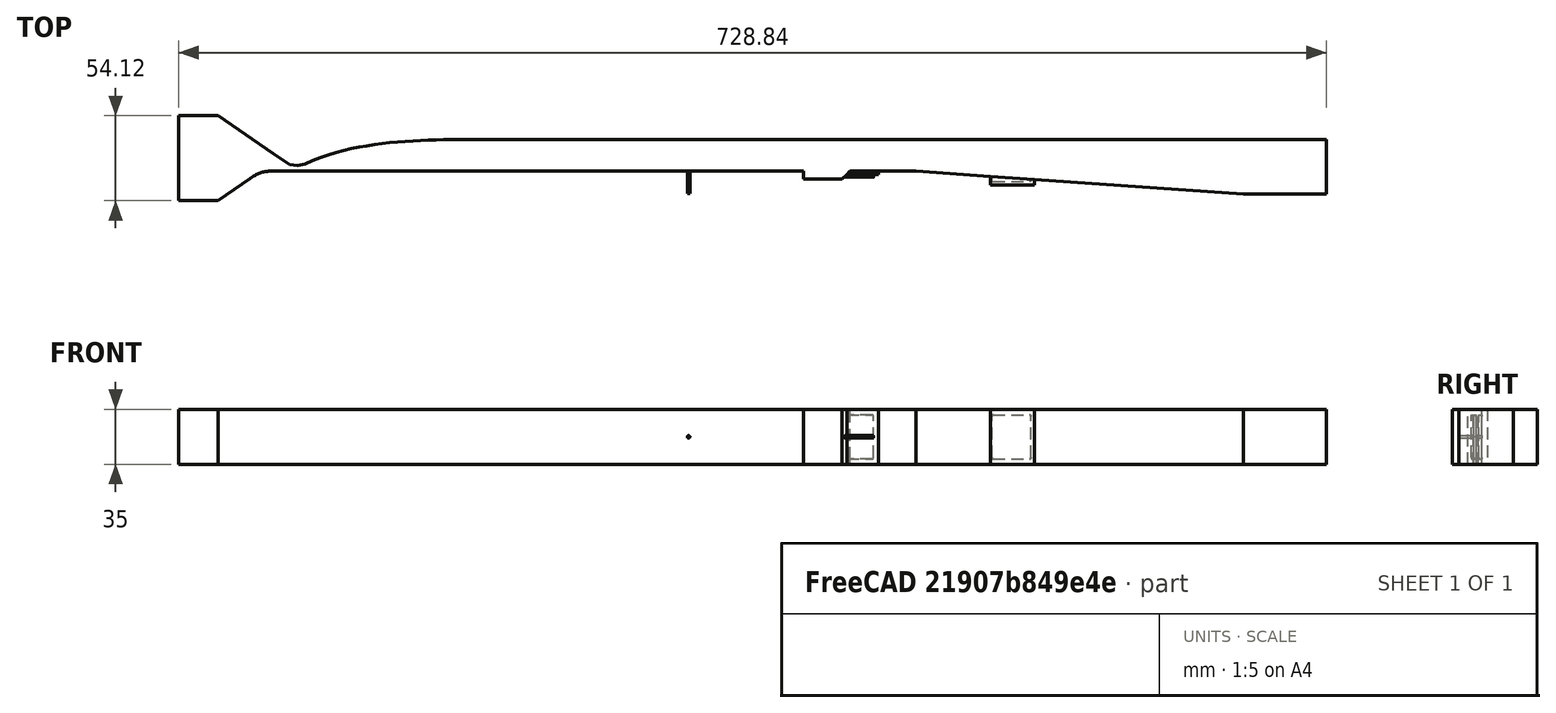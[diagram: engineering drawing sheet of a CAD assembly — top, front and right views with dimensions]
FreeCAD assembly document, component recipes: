
FREECAD ASSEMBLY — COMPONENT RECIPES ("actii")

This assembly document has 6 components, labeled P0..P5 below (a component is one placed body or linked part). 4 of them carry a construction recipe — the FreeCAD feature program that regenerates the part from scratch, quoted from this document or its linked companion documents; the rest are supplied as boundary geometry only. No exploded tour is included for this assembly.
COMPONENT P0 — recipe-attached ("Fluid001", modeled in this document).
Construction recipe (the document's own serialized feature program — sketch geometry with constraints, then the solid features built on it; lengths are millimeters unless a unit is written):

FEATURE [Sketcher::SketchObject] Sketch002  label="Fluid2DProfile001"
  FullyConstrained = true
  MapMode = 5
  Support = -> [XY_Plane001]
  sketch-geometry (16):
    g0: LineSegment StartX=209.437 StartY=27.0645 StartZ=0 EndX=234.437 EndY=27.0645 EndZ=0
    g1: BSplineCurve PolesCount=155 KnotsCount=153 Degree=3 IsPeriodic=0
    g2: LineSegment StartX=209.437 StartY=-27.0645 StartZ=0 EndX=234.437 EndY=-27.0645 EndZ=0
    g3: BSplineCurve PolesCount=28 KnotsCount=26 Degree=3 IsPeriodic=0
    g4: LineSegment StartX=383.28 StartY=11.6755 StartZ=0 EndX=938.28 EndY=11.6755 EndZ=0
    g5: LineSegment StartX=606.28 StartY=-8.32451 StartZ=0 EndX=606.28 EndY=-13.3245 EndZ=0
    g6: LineSegment StartX=606.28 StartY=-13.3245 StartZ=0 EndX=630.78 EndY=-13.3245 EndZ=0
    g7: LineSegment StartX=630.78 StartY=-13.3245 StartZ=0 EndX=635.78 EndY=-8.32451 EndZ=0
    g8: LineSegment StartX=635.78 StartY=-8.32451 StartZ=0 EndX=677.78 EndY=-8.32451 EndZ=0
    g9: LineSegment StartX=677.78 StartY=-8.32451 StartZ=0 EndX=885.78 EndY=-22.8693 EndZ=0
    g10: LineSegment StartX=938.28 StartY=11.6755 StartZ=0 EndX=938.28 EndY=-22.8693 EndZ=0
    g11: LineSegment StartX=885.78 StartY=-22.8693 StartZ=0 EndX=938.28 EndY=-22.8693 EndZ=0
    g12: LineSegment StartX=274.611 StartY=-8.32451 StartZ=0 EndX=606.28 EndY=-8.32451 EndZ=0
    g13: LineSegment StartX=269.437 StartY=2.95465 StartZ=0 EndX=234.437 EndY=27.0645 EndZ=0
    g14: LineSegment StartX=209.437 StartY=27.0645 StartZ=0 EndX=209.437 EndY=-27.0645 EndZ=0
    g15: LineSegment StartX=234.437 StartY=-27.0645 StartZ=0 EndX=254.652 EndY=-13.0512 EndZ=0
  constraints (44):
    c: Block(g1)
    c: Block(g3)
    c: DistanceX(g1,g4) = 555  'iso+cav+comb'
    c: Coincident(g4,g10)
    c: Vertical(g10)
    c: Coincident(g11,g10)
    c: Horizontal(g11)
    c: Coincident(g9,g8)
    c: Horizontal(g8)
    c: Horizontal(g6)
    c: Vertical(g5)
    c: Coincident(g11,g9)
    c: DistanceY(g5,g1) = 20
    c: Coincident(g8,g7)
    c: Horizontal(g4)
    c: DistanceX(g1,g5) = 223
    c: Coincident(g5,g6)
    c: DistanceX(g5,g6) = 24.5
    c: Coincident(g6,g7)
    c: DistanceX(g6,g7) = 5
    c: DistanceX(g5,g8) = 71.5
    c: Angle(g9,g4) = 0.0698132
    c: DistanceY(g5,g5) = 5
    c: DistanceY(g6,g7) = 5
    c: Coincident(g4,g1)
    c: DistanceX(g8,g9) = 208
    c: DistanceX(g0,g1) = 35
    c: DistanceX(g0,g0) = 25
    c: DistanceX(g2,g2) = 25
    c: Coincident(g12,g3)
    c: Coincident(g12,g5)
    c: Horizontal(g12)
    c: Coincident(g13,g1)
    c: Coincident(g13,g0)
    c: Coincident(g14,g0)
    c: Coincident(g14,g2)
    c: Vertical(g14)
    c: Coincident(g15,g2)
    c: Coincident(g15,g3)
    c: DistanceX(g2,g3) = 20.2152
    c: DistanceY(g2,g3) = 14.0133
    c: DistanceY(g1,g0) = 24.1099
    c: Horizontal(g0)
    c: Horizontal(g2)
FEATURE [PartDesign::Pad] Pad003
  AllowMultiFace = false
  Direction = (0,0,1)
  Length = 35
  Length2 = 100
  Midplane = true
  Profile = -> Sketch002
  Type = 0
FEATURE [PartDesign::Body] Body001  label="Fluid"
  Group = -> [Sketch002,Pad003]
  Origin = -> Origin001
  Tip = -> Pad003
COMPONENT P1 — same part as P0; its construction recipe is shown at P0.
COMPONENT P2 — geometry summary ("wallSample001"; no construction recipe available for this part):
  bounding box: 28.0 x 16.8 x 1.8 mm
  tessellated surface: 68 triangles
  volume: 801 mm^3 (95% of its bounding box)
  symmetry: mirror-symmetric across its z mid-plane
COMPONENT P3 — same part as P0; its construction recipe is shown at P0.
COMPONENT P4 — same part as P0; its construction recipe is shown at P0.
COMPONENT P5 — geometry summary ("WallSampleComb001"; no construction recipe available for this part):
  bounding box: 28.0 x 25.0 x 3.3 mm
  tessellated surface: 100 triangles
  volume: 1709 mm^3 (74% of its bounding box)
  symmetry: mirror-symmetric across its z mid-plane
PROVENANCE & LICENSES
A FreeCAD (.FCStd) document from a public repository crawl; recipes are the document's own serialized feature recipes (and, for linked parts, companion documents' recipes).
License: as declared in the source repository (recorded in the dataset sidecar).
